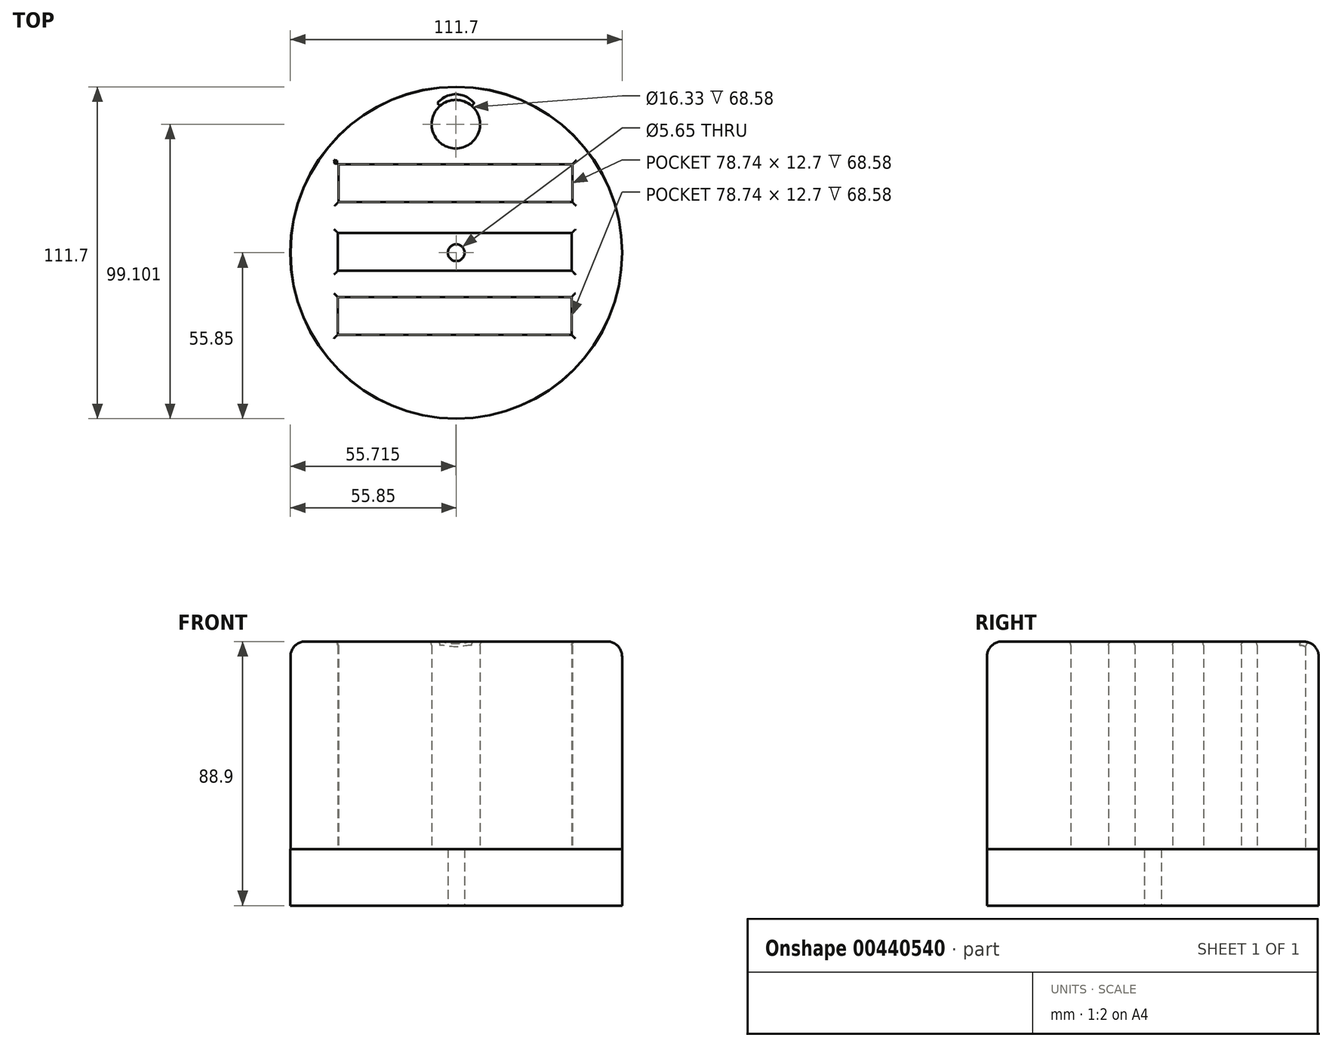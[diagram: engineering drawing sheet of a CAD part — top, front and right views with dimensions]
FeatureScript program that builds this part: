
annotation { "Feature Type Name" : "Feature", "Feature Type Description" : "" }
export const myFeature = defineFeature(function(context is Context, id is Id, definition is map)
    precondition{}
    {
        {
            var Q0;
            Q0=qCreatedBy(makeId("Top.planeOp"),FACE);
            var sketch = newSketch(context, id + "F0", { "sketchPlane" : qUnion([Q0])});
            skCircle(sketch, "E0", {"center": v(0, 0) * mm, "radius": 55.82 * mm});
            skLineSegment(sketch, "E1.bottom", {"start": v(-39.67, 29.74) * mm, "end": v(39.07, 29.74) * mm});
            skLineSegment(sketch, "E1.top", {"start": v(-39.67, 17.04) * mm, "end": v(39.07, 17.04) * mm});
            skLineSegment(sketch, "E1.left", {"start": v(-39.67, 29.74) * mm, "end": v(-39.67, 17.04) * mm});
            skLineSegment(sketch, "E1.right", {"start": v(39.07, 29.74) * mm, "end": v(39.07, 17.04) * mm});
            skLineSegment(sketch, "E2.bottom", {"start": v(-39.82, 6.62) * mm, "end": v(38.92, 6.62) * mm});
            skLineSegment(sketch, "E2.top", {"start": v(-39.82, -6.08) * mm, "end": v(38.92, -6.08) * mm});
            skLineSegment(sketch, "E2.left", {"start": v(-39.82, 6.62) * mm, "end": v(-39.82, -6.08) * mm});
            skLineSegment(sketch, "E2.right", {"start": v(38.92, 6.62) * mm, "end": v(38.92, -6.08) * mm});
            skLineSegment(sketch, "E3.bottom", {"start": v(-39.92, -14.92) * mm, "end": v(38.82, -14.92) * mm});
            skLineSegment(sketch, "E3.top", {"start": v(-39.92, -27.62) * mm, "end": v(38.82, -27.62) * mm});
            skLineSegment(sketch, "E3.left", {"start": v(-39.92, -14.92) * mm, "end": v(-39.92, -27.62) * mm});
            skLineSegment(sketch, "E3.right", {"start": v(38.82, -14.92) * mm, "end": v(38.82, -27.62) * mm});
            skCircle(sketch, "E4", {"center": v(-0.13, 43.25) * mm, "radius": 8.16 * mm});
            skSolve(sketch);
        }
        {
            var Q0;
            Q0=makeQuery(id+"F0.imprint","IMPRINT",FACE,{"disambiguationData":[TD([[makeQuery(id+"F0.imprint","IMPRINT",EDGE,{"derivedFrom":sQuery(id+"F0.wireOp",EDGE,"E0")}),1.0]])]});
            var Q1;
            Q1=sQuery(id+"F0.wireOp",EDGE,"E0");
            extrude(context, id + "F1", {"entities" : qUnion([Q0]), "surfaceEntities" : qUnion([Q1]), "depth" : 88.9 * mm});
        }
        {
            var Q0;
            Q0=makeQuery(id+"F1.opExtrude","CAP_EDGE",EDGE,{"disambiguationData":[OSD([sQuery(id+"F0.wireOp",EDGE,"E0")])],"isStart":false});
            fillet(context, id + "F2", {"entities" : qUnion([Q0]), "radius" : 5.08 * mm, "tangentPropagation" : true, "allowEdgeOverflow" : false});
        }
        {
            var Q0;
            Q0=makeQuery(id+"F1.opExtrude","CAP_EDGE",EDGE,{"disambiguationData":[OSD([sQuery(id+"F0.wireOp",EDGE,"E1.bottom")])],"isStart":false});
            var Q1;
            Q1=makeQuery(id+"F1.opExtrude","CAP_EDGE",EDGE,{"disambiguationData":[OSD([sQuery(id+"F0.wireOp",EDGE,"E1.left")])],"isStart":false});
            var Q2;
            Q2=makeQuery(id+"F1.opExtrude","CAP_EDGE",EDGE,{"disambiguationData":[OSD([sQuery(id+"F0.wireOp",EDGE,"E1.top")])],"isStart":false});
            var Q3;
            Q3=makeQuery(id+"F1.opExtrude","CAP_EDGE",EDGE,{"disambiguationData":[OSD([sQuery(id+"F0.wireOp",EDGE,"E1.right")])],"isStart":false});
            var Q4;
            Q4=makeQuery(id+"F1.opExtrude","CAP_EDGE",EDGE,{"disambiguationData":[OSD([sQuery(id+"F0.wireOp",EDGE,"E2.bottom")])],"isStart":false});
            var Q5;
            Q5=makeQuery(id+"F1.opExtrude","CAP_EDGE",EDGE,{"disambiguationData":[OSD([sQuery(id+"F0.wireOp",EDGE,"E2.left")])],"isStart":false});
            var Q6;
            Q6=makeQuery(id+"F1.opExtrude","CAP_EDGE",EDGE,{"disambiguationData":[OSD([sQuery(id+"F0.wireOp",EDGE,"E2.top")])],"isStart":false});
            var Q7;
            Q7=makeQuery(id+"F1.opExtrude","CAP_EDGE",EDGE,{"disambiguationData":[OSD([sQuery(id+"F0.wireOp",EDGE,"E2.right")])],"isStart":false});
            var Q8;
            Q8=makeQuery(id+"F1.opExtrude","CAP_EDGE",EDGE,{"disambiguationData":[OSD([sQuery(id+"F0.wireOp",EDGE,"E3.bottom")])],"isStart":false});
            var Q9;
            Q9=makeQuery(id+"F1.opExtrude","CAP_EDGE",EDGE,{"disambiguationData":[OSD([sQuery(id+"F0.wireOp",EDGE,"E3.left")])],"isStart":false});
            var Q10;
            Q10=makeQuery(id+"F1.opExtrude","CAP_EDGE",EDGE,{"disambiguationData":[OSD([sQuery(id+"F0.wireOp",EDGE,"E3.top")])],"isStart":false});
            var Q11;
            Q11=makeQuery(id+"F1.opExtrude","CAP_EDGE",EDGE,{"disambiguationData":[OSD([sQuery(id+"F0.wireOp",EDGE,"E3.right")])],"isStart":false});
            fillet(context, id + "F3", {"entities" : qUnion([Q0, Q1, Q2, Q3, Q4, Q5, Q6, Q7, Q8, Q9, Q10, Q11]), "radius" : 1.27 * mm, "tangentPropagation" : true, "allowEdgeOverflow" : false});
        }
        {
            var Q0;
            Q0=qCreatedBy(makeId("Top.planeOp"),FACE);
            var sketch = newSketch(context, id + "F4", { "sketchPlane" : qUnion([Q0])});
            skCircle(sketch, "E5", {"center": v(0, 0) * mm, "radius": 55.85 * mm});
            skCircle(sketch, "E6.0", {"center": v(0, 0) * mm, "radius": 2.83 * mm});
            skSolve(sketch);
        }
        {
            var Q0;
            Q0 = qSketchRegion(id + "F4", true);
            extrude(context, id + "F5", {"entities" : qUnion([Q0]), "operationType" : NewBodyOperationType.ADD, "depth" : 19.05 * mm});
        }
        {
            var Q0;
            Q0=makeQuery(id+"F1.opExtrude","CAP_EDGE",EDGE,{"disambiguationData":[OSD([sQuery(id+"F0.wireOp",EDGE,"E4")])],"isStart":false});
            fillet(context, id + "F6", {"entities" : qUnion([Q0]), "radius" : 1.27 * mm, "tangentPropagation" : true, "allowEdgeOverflow" : false});
        }
    });
